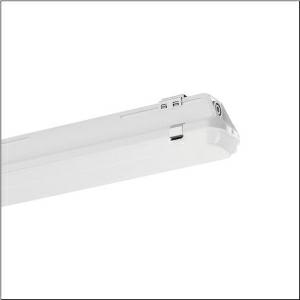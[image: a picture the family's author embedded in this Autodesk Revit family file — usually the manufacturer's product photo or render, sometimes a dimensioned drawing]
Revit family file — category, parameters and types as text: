
# Revit family: monsun_r__21_emergency_51fb10dp468b2_8461
name_source: partatom
category: Lighting Fixtures
units: mm (PartAtom-declared; Revit-internal decimal feet)

## family parameters
Cut with Voids When Loaded = No
Host = Face
Light Source = No
Part Type = Normal
Room Calculation Point = No
Round Connector Dimension = Use Diameter
Shared = No

## types (1)
- --- (1 x LED, 940 lm, 7.3 W, 4000K)
    Apparent Load = 7 VA
    CIE Flux Codes = 47 77 93 94 100
    Color Rendering = 80
    Color Temperature = 4000K
    Default Elevation = 1800 mm
    Description = Monsun® 21 emergency, damp-proof luminaire, chain hanger, primary optical cover: enclosure, of PMMA, light emission: direct distribution, primary light characteristic: symmetric, installation type: suspended mounting, surface-mounted, horizontal mounting, vertical mounting, LED, rated luminous flux: 6.060lm, luminous efficacy: 154lm/W, light colour: 840, colour temperature: 4000K, control gear: ECG DALI, with terminal, 5-pole, max. 2.5mm², mains connection: 220..240V, AC/DC, 0/50..60Hz, rated input power: 39W, housing, of glass-fibre reinforced polyester, uncoated, bright grey, length: 1.590mm, width: 90mm, height: 88mm, clip for enclosure, of stainless steel (V2A), ceiling mounting element, of stainless steel (V2A), chain hanger, of stainless steel (V2A), protection rating (complete): IP66, insulation class (complete): insulation class I (protective earthing), certification: CE, protection symbol: D, impact resistance: IK04, permissible operating ambient temperature: -25..+35°C, standard: EN 50419, EN 60598-2-1, EN 60598-2-22, corresponds to IFS (International Featured Standards) requirements for safety and quality in the food industry, for indoor or canopied outdoor use, no direct snow, no direct sun, no direct rain, packaging unit: 1 piece
    Height = 89 mm
    Lamp = 1 x LED
    Lamp Light Flux = 940 lm
    Lamp Power = 7.3 W
    Lamp count = 1
    Length = 1590 mm
    Luminous efficacy = 129 lm/W
    Manufacturer = Siteco
    ModVariant = No
    Model = 51FB10DP468B2
    Mounting Place = Ceiling
    Mounting Type = Pendant
    Number of Poles = 1
    OnlyDefault = Yes
    Power Factor = 1
    Product Name = Monsun® 21 emergency
    Product group = damp-proof luminaire | ceiling pendant
    ProductGroupID = 908
    Protection Class = Protection class I
    Protection Degree = IP 66
    RLX_Detail_Level = 1
    RlxData = <blob elided: 91985 chars, md5=696b07bb>
    Socket = socket
    Standby Power = 0 W
    System Light Flux = 940 lm
    System Power = 7 W
    Type Comments = : equivalent power supply (DC)
    Type Image = l_1006717.jpg
    URL = http://relux.com
    VarID = @adj_124957
    Voltage = 0 V
    Weight = 0.00 kg
    Width = 90 mm

## geometry (parser evidence)
native form markers: Blend x4, Sweep x14
no freeform markers — native parametric forms only
